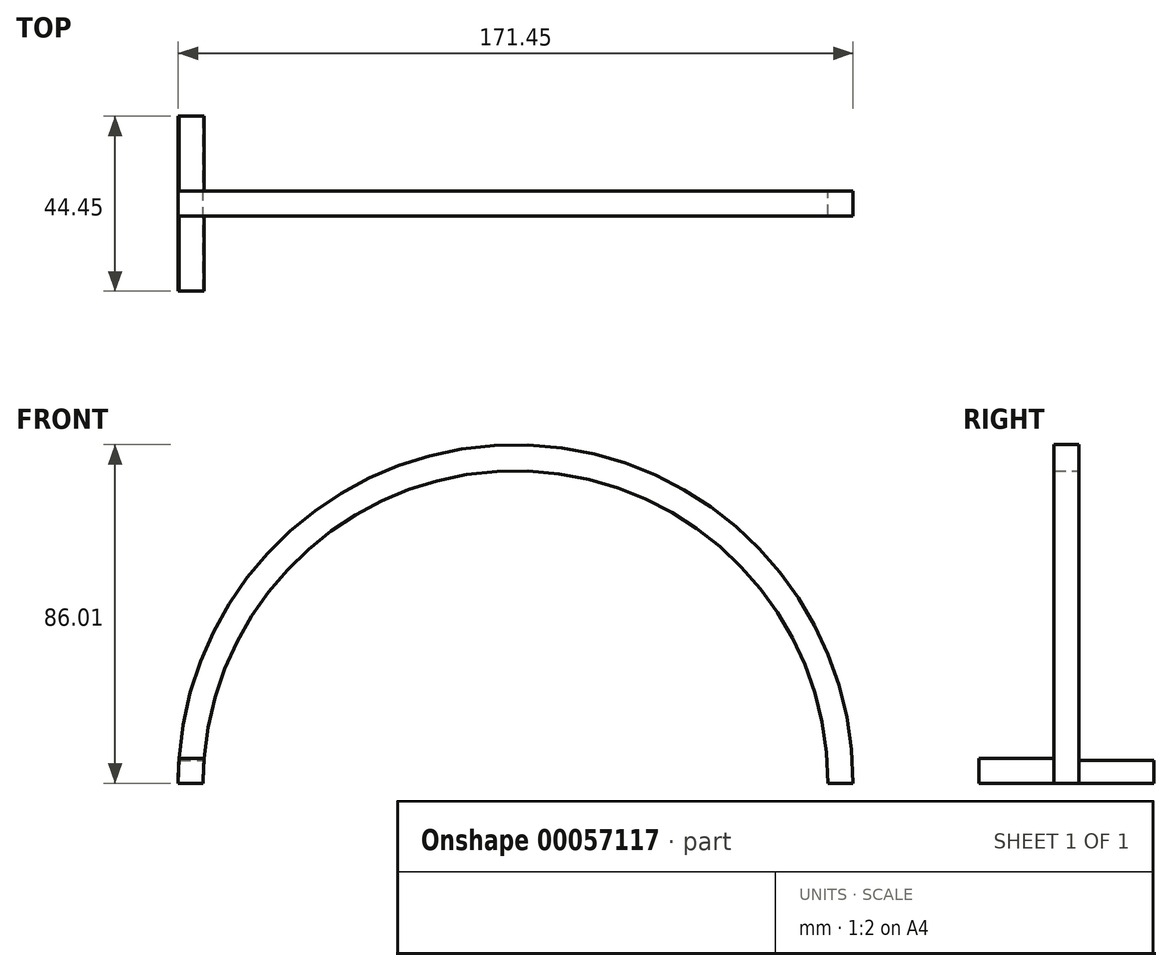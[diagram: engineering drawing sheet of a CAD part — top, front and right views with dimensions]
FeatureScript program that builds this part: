
annotation { "Feature Type Name" : "Feature", "Feature Type Description" : "" }
export const myFeature = defineFeature(function(context is Context, id is Id, definition is map)
    precondition{}
    {
        {
            var Q0;
            Q0=qCreatedBy(makeId("Front.planeOp"),FACE);
            var sketch = newSketch(context, id + "F0", { "sketchPlane" : qUnion([Q0])});
            skArc(sketch, "E0", {"start": v(88.51, 0) * mm, "mid": v(9.14, 79.37) * mm, "end": v(-70.24, 0) * mm});
            skLineSegment(sketch, "E1", {"start": v(-70.24, 0) * mm, "end": v(-76.59, 0) * mm});
            skLineSegment(sketch, "E2", {"start": v(88.51, 0) * mm, "end": v(94.86, 0) * mm});
            skArc(sketch, "E3", {"start": v(94.86, 0) * mm, "mid": v(9.14, 86) * mm, "end": v(-76.59, 0) * mm});
            skSolve(sketch);
        }
        {
            var Q0;
            Q0=makeQuery(id+"F0.imprint","IMPRINT",FACE,{"disambiguationData":[TD([[makeQuery(id+"F0.imprint","IMPRINT",EDGE,{"derivedFrom":sQuery(id+"F0.wireOp",EDGE,"E0")}),-1.0]])]});
            extrude(context, id + "F1", {"entities" : qUnion([Q0]), "depth" : 6.35 * mm});
        }
        {
            var Q0;
            Q0=makeQuery(id+"F1.opExtrude","CAP_FACE",FACE,{"disambiguationData":[OSD([sQuery(id+"F0.wireOp",EDGE,"E0"),sQuery(id+"F0.wireOp",EDGE,"E1"),sQuery(id+"F0.wireOp",EDGE,"E2"),sQuery(id+"F0.wireOp",EDGE,"E3")])],"isStart":false});
            var sketch = newSketch(context, id + "F2", { "sketchPlane" : qUnion([Q0])});
            skLineSegment(sketch, "E4", {"start": v(-70.24, 0) * mm, "end": v(-76.59, 0) * mm});
            skLineSegment(sketch, "E5", {"start": v(-70.24, 0) * mm, "end": v(-69.98, 6.37) * mm});
            skLineSegment(sketch, "E6", {"start": v(-69.98, 6.37) * mm, "end": v(-76.37, 6.37) * mm});
            skLineSegment(sketch, "E7", {"start": v(-76.37, 6.37) * mm, "end": v(-76.59, 0) * mm});
            skSolve(sketch);
        }
        {
            var Q0;
            {var subQ0=sQuery(id+"F2.wireOp",EDGE,"E4");Q0=makeQuery(id+"F2.imprint","IMPRINT",FACE,{"disambiguationData":[TD([[makeQuery(id+"F2.imprint","IMPRINT",EDGE,{"derivedFrom":subQ0}),-1.0]])]});}
            extrude(context, id + "F3", {"entities" : qUnion([Q0]), "operationType" : NewBodyOperationType.ADD, "depth" : 19.05 * mm});
        }
        {
            var Q0;
            Q0=makeQuery(id+"F1.opExtrude","CAP_FACE",FACE,{"disambiguationData":[OSD([sQuery(id+"F0.wireOp",EDGE,"E0"),sQuery(id+"F0.wireOp",EDGE,"E1"),sQuery(id+"F0.wireOp",EDGE,"E2"),sQuery(id+"F0.wireOp",EDGE,"E3")])],"isStart":true});
            var sketch = newSketch(context, id + "F4", { "sketchPlane" : qUnion([Q0])});
            skLineSegment(sketch, "E8", {"start": v(70.24, 0) * mm, "end": v(76.59, 0) * mm});
            skLineSegment(sketch, "E9", {"start": v(76.59, 0) * mm, "end": v(76.41, 5.8) * mm});
            skLineSegment(sketch, "E10", {"start": v(76.41, 5.8) * mm, "end": v(70.03, 5.8) * mm});
            skLineSegment(sketch, "E11", {"start": v(70.03, 5.8) * mm, "end": v(70.24, 0) * mm});
            skSolve(sketch);
        }
        {
            var Q0;
            {var subQ0=sQuery(id+"F4.wireOp",EDGE,"E8");Q0=makeQuery(id+"F4.imprint","IMPRINT",FACE,{"disambiguationData":[TD([[makeQuery(id+"F4.imprint","IMPRINT",EDGE,{"derivedFrom":subQ0}),1.0]])]});}
            extrude(context, id + "F5", {"entities" : qUnion([Q0]), "operationType" : NewBodyOperationType.ADD, "depth" : 19.05 * mm});
        }
    });
